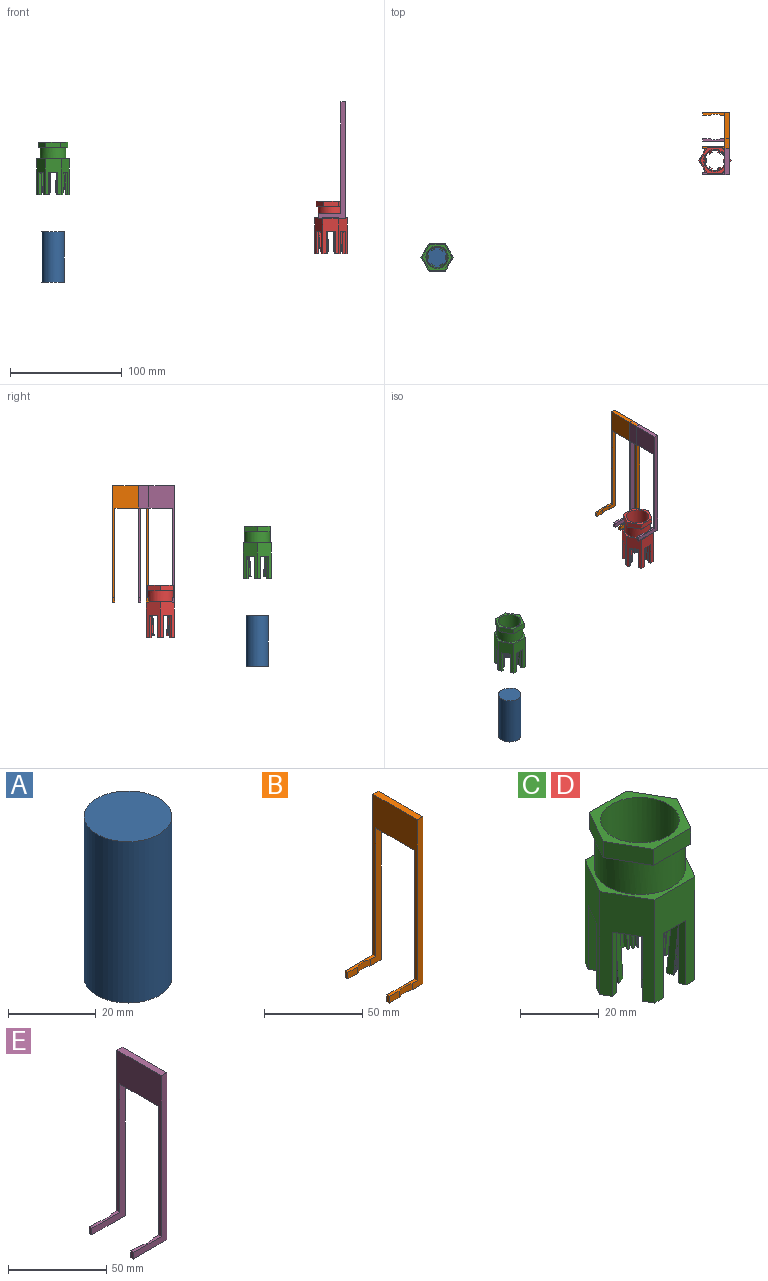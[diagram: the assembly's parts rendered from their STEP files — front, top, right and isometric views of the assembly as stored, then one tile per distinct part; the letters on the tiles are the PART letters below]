
ASSEMBLY  parts=5 mates=3
PART A: 3 faces, bbox 20x20x45 mm
  f0: cylinder r=10mm len=45mm, axis (0,0,-1), area 2827.4mm2, adj f1,f2
  f1: plane 20x20mm, normal (0,0,1), area 314.2mm2, adj f0
  f2: plane 20x20mm, normal (0,0,-1), area 314.2mm2, adj f0
PART B: 18 faces, bbox 24x32x104 mm
  f0: plane 84x7.81mm, normal (0,-1,0), area 351.2mm2, adj f1,f2,f6,f7,f8,f17
  f1: cylinder r=11.5mm len=9.38mm, axis (0,0,-1), area 38.7mm2, adj f0,f5,f6,f7
  f2: plane 104x32mm, normal (1,0,0), area 976mm2, adj f0,f3,f7,f9,f10,f14,f16,f17
  f3: plane 104x24mm, normal (0,1,0), area 496mm2, adj f2,f4,f6,f7,f8,f9
  f4: plane 4x2mm, normal (-1,0,0), area 8mm2, adj f3,f5,f6,f7
  f5: plane 6.81x4mm, normal (0,-1,0), area 27.2mm2, adj f1,f4,f6,f7
  f6: plane 20x2mm, normal (0,0,1), area 33.7mm2, adj f0,f1,f3,f4,f5,f8
  f7: plane 24x2mm, normal (0,0,-1), area 41.7mm2, adj f0,f1,f2,f3,f4,f5
  f8: plane 100x32mm, normal (-1,0,0), area 960mm2, adj f0,f3,f6,f9,f10,f14,f15,f17
  f9: plane 32x4mm, normal (0,0,1), area 128mm2, adj f2,f3,f8,f14
  f10: plane 84x24mm, normal (0,1,0), area 416mm2, adj f2,f8,f11,f15,f16,f17
  f11: plane 4x2mm, normal (-1,0,0), area 8mm2, adj f10,f12,f15,f16
  f12: plane 6.81x4mm, normal (0,-1,0), area 27.2mm2, adj f11,f13,f15,f16
  f13: cylinder r=11.5mm len=9.38mm, axis (0,0,-1), area 38.7mm2, adj f12,f14,f15,f16
  f14: plane 104x7.81mm, normal (0,-1,0), area 431.2mm2, adj f2,f8,f9,f13,f15,f16
  f15: plane 20x2mm, normal (0,0,1), area 33.7mm2, adj f8,f10,f11,f12,f13,f14
  f16: plane 24x2mm, normal (0,0,-1), area 41.7mm2, adj f2,f10,f11,f12,f13,f14
  f17: plane 28x4mm, normal (0,0,-1), area 112mm2, adj f0,f2,f8,f10
PART C: 256 faces, bbox 28.9x25x47 mm
  f0: plane 5.47x4.34mm, normal (0,0,-1), area 11.8mm2, adj f14,f17,f114,f115,f226,f239
  f1: plane 5.47x4.34mm, normal (0,0,-1), area 11.8mm2, adj f14,f16,f35,f37,f236,f241
  f2: cone r=9.54mm half-angle=5deg, axis (0,0,1), area 7.3mm2, adj f12,f16,f190,f241
  f3: plane 10x1.51mm, normal (0.98,-0.17,0), area 11mm2, adj f13,f18,f133,f240
  f4: plane 10x1.41mm, normal (-1,0.09,0), area 9.8mm2, adj f15,f18,f133,f240
  f5: plane 10x1.69mm, normal (-0.97,0.26,0), area 13.1mm2, adj f13,f17,f132,f240
  f6: plane 10x1.51mm, normal (0.98,0.17,0), area 11mm2, adj f10,f20,f135,f240
  f7: plane 10x1.69mm, normal (-0.97,-0.26,0), area 13.1mm2, adj f11,f20,f135,f240
  f8: plane 10x1.38mm, normal (1,0,0), area 9.4mm2, adj f15,f19,f134,f240
  f9: plane 10x1.41mm, normal (-1,-0.09,0), area 9.8mm2, adj f10,f19,f134,f240
  f10: cone r=10mm half-angle=5deg, axis (0,0,1), area 8.4mm2, adj f6,f9,f216,f240
  f11: cone r=10mm half-angle=5deg, axis (0,0,1), area 14.3mm2, adj f7,f12,f190,f216,f240,f241
  f12: cone r=7.55mm half-angle=85deg, axis (0,0,-1), area 0.7mm2, adj f2,f11,f190,f241
  f13: cone r=10mm half-angle=5deg, axis (0,0,1), area 8.4mm2, adj f3,f5,f216,f240
  f14: plane 32x14.43mm, normal (0,-1,0), area 301.9mm2, adj f0,f1,f35,f114,f217,f239,f240,f241
  f15: cone r=10mm half-angle=5deg, axis (0,0,1), area 8.4mm2, adj f4,f8,f216,f240
  f16: plane 30.04x2.75mm, normal (0,1,0), area 74mm2, adj f1,f2,f37,f120,f136,f137,f190,f191
  f17: plane 30x3.25mm, normal (0,1,0), area 78.7mm2, adj f0,f5,f115,f131,f132,f167,f168,f169
  f18: plane 10x0.93mm, normal (0,1,0), area 9.3mm2, adj f3,f4,f133,f240
  f19: plane 10x0.92mm, normal (0,1,0), area 9.2mm2, adj f8,f9,f134,f240
  f20: plane 10x0.96mm, normal (0,1,0), area 9.6mm2, adj f6,f7,f135,f240
  f21: plane 5.57x3.66mm, normal (0,0,-1), area 11.8mm2, adj f35,f36,f55,f57,f233,f238
  f22: cone r=9.54mm half-angle=5deg, axis (0,0,1), area 7.3mm2, adj f34,f36,f186,f238
  f23: plane 10x1.44mm, normal (0.34,0.94,0), area 11mm2, adj f32,f40,f141,f237
  f24: plane 10x1.69mm, normal (-0.26,-0.97,0), area 13.1mm2, adj f33,f40,f141,f237
  f25: plane 10x1.19mm, normal (0.5,0.87,0), area 9.4mm2, adj f31,f39,f140,f237
  f26: plane 10x1.28mm, normal (-0.42,-0.91,0), area 9.8mm2, adj f32,f39,f140,f237
  f27: plane 10x1.18mm, normal (0.64,0.77,0), area 11mm2, adj f30,f38,f139,f237
  f28: plane 10x1.16mm, normal (-0.57,-0.82,0), area 9.8mm2, adj f31,f38,f139,f237
  f29: plane 10x1.23mm, normal (-0.71,-0.71,0), area 13.1mm2, adj f30,f37,f138,f237
  f30: cone r=10mm half-angle=5deg, axis (0,0,1), area 8.4mm2, adj f27,f29,f216,f237
  f31: cone r=10mm half-angle=5deg, axis (0,0,1), area 8.4mm2, adj f25,f28,f216,f237
  f32: cone r=10mm half-angle=5deg, axis (0,0,1), area 8.4mm2, adj f23,f26,f216,f237
  f33: cone r=10mm half-angle=5deg, axis (0,0,1), area 14.3mm2, adj f24,f34,f186,f216,f237,f238
  f34: cone r=7.55mm half-angle=85deg, axis (0,0,-1), area 0.7mm2, adj f22,f33,f186,f238
  f35: plane 32x12.5mm, normal (0.87,-0.5,0), area 301.9mm2, adj f1,f14,f21,f55,f217,f236,f237,f238
  f36: plane 30.04x2.38mm, normal (-0.87,0.5,0), area 74mm2, adj f21,f22,f57,f122,f142,f143,f186,f187
  f37: plane 30x2.81mm, normal (-0.87,0.5,0), area 78.7mm2, adj f1,f16,f29,f121,f137,f138,f188,f189
  f38: plane 10x0.81mm, normal (-0.87,0.5,0), area 9.3mm2, adj f27,f28,f139,f237
  f39: plane 10x0.8mm, normal (-0.87,0.5,0), area 9.2mm2, adj f25,f26,f140,f237
  f40: plane 10x0.83mm, normal (-0.87,0.5,0), area 9.6mm2, adj f23,f24,f141,f237
  f41: plane 5.47x4.34mm, normal (0,0,-1), area 11.8mm2, adj f55,f56,f75,f77,f230,f235
  f42: cone r=9.54mm half-angle=5deg, axis (0,0,1), area 7.3mm2, adj f54,f56,f182,f235
  f43: plane 10x1.18mm, normal (-0.64,0.77,0), area 11mm2, adj f52,f60,f147,f234
  f44: plane 10x1.23mm, normal (0.71,-0.71,0), area 13.1mm2, adj f53,f60,f147,f234
  f45: plane 10x1.19mm, normal (-0.5,0.87,0), area 9.4mm2, adj f51,f59,f146,f234
  f46: plane 10x1.16mm, normal (0.57,-0.82,0), area 9.8mm2, adj f52,f59,f146,f234
  f47: plane 10x1.44mm, normal (-0.34,0.94,0), area 11mm2, adj f50,f58,f145,f234
  f48: plane 10x1.28mm, normal (0.42,-0.91,0), area 9.8mm2, adj f51,f58,f145,f234
  f49: plane 10x1.69mm, normal (0.26,-0.97,0), area 13.1mm2, adj f50,f57,f144,f234
  f50: cone r=10mm half-angle=5deg, axis (0,0,1), area 8.4mm2, adj f47,f49,f216,f234
  f51: cone r=10mm half-angle=5deg, axis (0,0,1), area 8.4mm2, adj f45,f48,f216,f234
  f52: cone r=10mm half-angle=5deg, axis (0,0,1), area 8.4mm2, adj f43,f46,f216,f234
  f53: cone r=10mm half-angle=5deg, axis (0,0,1), area 14.3mm2, adj f44,f54,f182,f216,f234,f235
  f54: cone r=7.55mm half-angle=85deg, axis (0,0,-1), area 0.7mm2, adj f42,f53,f182,f235
  f55: plane 32x12.5mm, normal (0.87,0.5,0), area 301.9mm2, adj f21,f35,f41,f75,f217,f233,f234,f235
  f56: plane 30.04x2.38mm, normal (-0.87,-0.5,0), area 74mm2, adj f41,f42,f77,f124,f148,f149,f182,f183
  f57: plane 30x2.81mm, normal (-0.87,-0.5,0), area 78.7mm2, adj f21,f36,f49,f123,f143,f144,f184,f185
  f58: plane 10x0.81mm, normal (-0.87,-0.5,0), area 9.3mm2, adj f47,f48,f145,f234
  f59: plane 10x0.8mm, normal (-0.87,-0.5,0), area 9.2mm2, adj f45,f46,f146,f234
  f60: plane 10x0.83mm, normal (-0.87,-0.5,0), area 9.6mm2, adj f43,f44,f147,f234
  f61: plane 5.47x4.34mm, normal (0,0,-1), area 11.8mm2, adj f75,f76,f95,f97,f227,f232
  f62: cone r=9.54mm half-angle=5deg, axis (0,0,1), area 7.3mm2, adj f74,f76,f178,f232
  f63: plane 10x1.51mm, normal (-0.98,-0.17,0), area 11mm2, adj f72,f80,f153,f231
  f64: plane 10x1.69mm, normal (0.97,0.26,0), area 13.1mm2, adj f73,f80,f153,f231
  f65: plane 10x1.38mm, normal (-1,0,0), area 9.4mm2, adj f71,f79,f152,f231
  f66: plane 10x1.41mm, normal (1,0.09,0), area 9.8mm2, adj f72,f79,f152,f231
  f67: plane 10x1.51mm, normal (-0.98,0.17,0), area 11mm2, adj f70,f78,f151,f231
  f68: plane 10x1.41mm, normal (1,-0.09,0), area 9.8mm2, adj f71,f78,f151,f231
  f69: plane 10x1.69mm, normal (0.97,-0.26,0), area 13.1mm2, adj f70,f77,f150,f231
  f70: cone r=10mm half-angle=5deg, axis (0,0,1), area 8.4mm2, adj f67,f69,f216,f231
  f71: cone r=10mm half-angle=5deg, axis (0,0,1), area 8.4mm2, adj f65,f68,f216,f231
  f72: cone r=10mm half-angle=5deg, axis (0,0,1), area 8.4mm2, adj f63,f66,f216,f231
  f73: cone r=10mm half-angle=5deg, axis (0,0,1), area 14.3mm2, adj f64,f74,f178,f216,f231,f232
  f74: cone r=7.55mm half-angle=85deg, axis (0,0,-1), area 0.7mm2, adj f62,f73,f178,f232
  f75: plane 32x14.43mm, normal (0,1,0), area 301.9mm2, adj f41,f55,f61,f95,f217,f230,f231,f232
  f76: plane 30.04x2.75mm, normal (0,-1,0), area 74mm2, adj f61,f62,f97,f126,f154,f155,f178,f179
  f77: plane 30x3.25mm, normal (0,-1,0), area 78.7mm2, adj f41,f56,f69,f125,f149,f150,f180,f181
  f78: plane 10x0.93mm, normal (0,-1,0), area 9.3mm2, adj f67,f68,f151,f231
  f79: plane 10x0.92mm, normal (0,-1,0), area 9.2mm2, adj f65,f66,f152,f231
  f80: plane 10x0.96mm, normal (0,-1,0), area 9.6mm2, adj f63,f64,f153,f231
  f81: plane 5.57x3.66mm, normal (0,0,-1), area 11.8mm2, adj f95,f96,f114,f116,f225,f229
  f82: cone r=9.54mm half-angle=5deg, axis (0,0,1), area 7.3mm2, adj f94,f96,f174,f229
  f83: plane 10x1.44mm, normal (-0.34,-0.94,0), area 11mm2, adj f92,f100,f159,f228
  f84: plane 10x1.69mm, normal (0.26,0.97,0), area 13.1mm2, adj f93,f100,f159,f228
  f85: plane 10x1.19mm, normal (-0.5,-0.87,0), area 9.4mm2, adj f91,f99,f158,f228
  f86: plane 10x1.28mm, normal (0.42,0.91,0), area 9.8mm2, adj f92,f99,f158,f228
  f87: plane 10x1.18mm, normal (-0.64,-0.77,0), area 11mm2, adj f90,f98,f157,f228
  f88: plane 10x1.16mm, normal (0.57,0.82,0), area 9.8mm2, adj f91,f98,f157,f228
  f89: plane 10x1.23mm, normal (0.71,0.71,0), area 13.1mm2, adj f90,f97,f156,f228
  f90: cone r=10mm half-angle=5deg, axis (0,0,1), area 8.4mm2, adj f87,f89,f216,f228
  f91: cone r=10mm half-angle=5deg, axis (0,0,1), area 8.4mm2, adj f85,f88,f216,f228
  f92: cone r=10mm half-angle=5deg, axis (0,0,1), area 8.4mm2, adj f83,f86,f216,f228
  f93: cone r=10mm half-angle=5deg, axis (0,0,1), area 14.3mm2, adj f84,f94,f174,f216,f228,f229
  f94: cone r=7.55mm half-angle=85deg, axis (0,0,-1), area 0.7mm2, adj f82,f93,f174,f229
  f95: plane 32x12.5mm, normal (-0.87,0.5,0), area 301.9mm2, adj f61,f75,f81,f114,f217,f227,f228,f229
  f96: plane 30.04x2.38mm, normal (0.87,-0.5,0), area 74mm2, adj f81,f82,f116,f128,f160,f161,f174,f175
  f97: plane 30x2.81mm, normal (0.87,-0.5,0), area 78.7mm2, adj f61,f76,f89,f127,f155,f156,f176,f177
  f98: plane 10x0.81mm, normal (0.87,-0.5,0), area 9.3mm2, adj f87,f88,f157,f228
  f99: plane 10x0.8mm, normal (0.87,-0.5,0), area 9.2mm2, adj f85,f86,f158,f228
  f100: plane 10x0.83mm, normal (0.87,-0.5,0), area 9.6mm2, adj f83,f84,f159,f228
  f101: cone r=9.54mm half-angle=5deg, axis (0,0,1), area 7.3mm2, adj f113,f115,f170,f226
  f102: plane 10x1.18mm, normal (0.64,-0.77,0), area 11mm2, adj f111,f119,f165,f224
  f103: plane 10x1.23mm, normal (-0.71,0.71,0), area 13.1mm2, adj f112,f119,f165,f224
  f104: plane 10x1.19mm, normal (0.5,-0.87,0), area 9.4mm2, adj f110,f118,f164,f224
  f105: plane 10x1.16mm, normal (-0.57,0.82,0), area 9.8mm2, adj f111,f118,f164,f224
  f106: plane 10x1.44mm, normal (0.34,-0.94,0), area 11mm2, adj f109,f117,f163,f224
  f107: plane 10x1.28mm, normal (-0.42,0.91,0), area 9.8mm2, adj f110,f117,f163,f224
  f108: plane 10x1.69mm, normal (-0.26,0.97,0), area 13.1mm2, adj f109,f116,f162,f224
  f109: cone r=10mm half-angle=5deg, axis (0,0,1), area 8.4mm2, adj f106,f108,f216,f224
  f110: cone r=10mm half-angle=5deg, axis (0,0,1), area 8.4mm2, adj f104,f107,f216,f224
  f111: cone r=10mm half-angle=5deg, axis (0,0,1), area 8.4mm2, adj f102,f105,f216,f224
  f112: cone r=10mm half-angle=5deg, axis (0,0,1), area 14.3mm2, adj f103,f113,f170,f216,f224,f226
  f113: cone r=7.55mm half-angle=85deg, axis (0,0,-1), area 0.7mm2, adj f101,f112,f170,f226
  f114: plane 32x12.5mm, normal (-0.87,-0.5,0), area 301.9mm2, adj f0,f14,f81,f95,f217,f224,f225,f226
  f115: plane 30.04x2.38mm, normal (0.87,0.5,0), area 74mm2, adj f0,f17,f101,f130,f166,f167,f170,f171
  f116: plane 30x2.81mm, normal (0.87,0.5,0), area 78.7mm2, adj f81,f96,f108,f129,f161,f162,f172,f173
  f117: plane 10x0.81mm, normal (0.87,0.5,0), area 9.3mm2, adj f106,f107,f163,f224
  f118: plane 10x0.8mm, normal (0.87,0.5,0), area 9.2mm2, adj f104,f105,f164,f224
  f119: plane 10x0.83mm, normal (0.87,0.5,0), area 9.6mm2, adj f102,f103,f165,f224
  f120: cone r=9.54mm half-angle=5deg, axis (0,0,1), area 24.6mm2, adj f16,f137,f191,f193,f223
  f121: cone r=9.54mm half-angle=5deg, axis (0,0,1), area 19.1mm2, adj f37,f188,f189,f195
  f122: cone r=9.54mm half-angle=5deg, axis (0,0,1), area 24.6mm2, adj f36,f143,f187,f197,f222
  f123: cone r=9.54mm half-angle=5deg, axis (0,0,1), area 19.1mm2, adj f57,f184,f185,f199
  f124: cone r=9.54mm half-angle=5deg, axis (0,0,1), area 24.6mm2, adj f56,f149,f183,f201,f221
  f125: cone r=9.54mm half-angle=5deg, axis (0,0,1), area 19.1mm2, adj f77,f180,f181,f203
  f126: cone r=9.54mm half-angle=5deg, axis (0,0,1), area 24.6mm2, adj f76,f155,f179,f205,f220
  f127: cone r=9.54mm half-angle=5deg, axis (0,0,1), area 19.1mm2, adj f97,f176,f177,f207
  f128: cone r=9.54mm half-angle=5deg, axis (0,0,1), area 24.6mm2, adj f96,f161,f175,f209,f219
  f129: cone r=9.54mm half-angle=5deg, axis (0,0,1), area 19.1mm2, adj f116,f172,f173,f211
  f130: cone r=9.54mm half-angle=5deg, axis (0,0,1), area 24.6mm2, adj f115,f167,f171,f213,f218
  f131: cone r=9.54mm half-angle=5deg, axis (0,0,1), area 19.1mm2, adj f17,f168,f169,f215
  f132: plane 1.23x1.1mm, normal (0,0,-1), area 0.9mm2, adj f5,f17,f168,f216
  f133: plane 0.98x0.65mm, normal (0,0,-1), area 0.5mm2, adj f3,f4,f18,f216
  f134: plane 0.92x0.54mm, normal (0,0,-1), area 0.5mm2, adj f8,f9,f19,f216
  f135: plane 1.08x0.84mm, normal (0,0,-1), area 0.7mm2, adj f6,f7,f20,f216
  f136: plane 1.48x1.44mm, normal (0,0,-1), area 1.3mm2, adj f16,f190,f191,f216
  f137: plane 2.31x1.65mm, normal (0,0,-1), area 1.8mm2, adj f16,f37,f120,f189,f216,f223
  f138: plane 1.49x1.26mm, normal (0,0,-1), area 0.9mm2, adj f29,f37,f188,f216
  f139: plane 1.12x0.97mm, normal (0,0,-1), area 0.5mm2, adj f27,f28,f38,f216
  f140: plane 1.02x0.89mm, normal (0,0,-1), area 0.5mm2, adj f25,f26,f39,f216
  f141: plane 1.1x1.06mm, normal (0,0,-1), area 0.7mm2, adj f23,f24,f40,f216
  f142: plane 1.69x1.07mm, normal (0,0,-1), area 1.3mm2, adj f36,f186,f187,f216
  f143: plane 2.16x1.22mm, normal (0,0,-1), area 1.8mm2, adj f36,f57,f122,f185,f216,f222
  f144: plane 1.35x1.08mm, normal (0,0,-1), area 0.9mm2, adj f49,f57,f184,f216
  f145: plane 1.03x0.96mm, normal (0,0,-1), area 0.5mm2, adj f47,f48,f58,f216
  f146: plane 1.05x0.9mm, normal (0,0,-1), area 0.5mm2, adj f45,f46,f59,f216
  f147: plane 1.26x1.1mm, normal (0,0,-1), area 0.7mm2, adj f43,f44,f60,f216
  f148: plane 1.83x1.45mm, normal (0,0,-1), area 1.3mm2, adj f56,f182,f183,f216
  f149: plane 1.95x1.84mm, normal (0,0,-1), area 1.8mm2, adj f56,f77,f124,f181,f216,f221
  f150: plane 1.23x1.1mm, normal (0,0,-1), area 0.9mm2, adj f69,f77,f180,f216
  f151: plane 0.98x0.65mm, normal (0,0,-1), area 0.5mm2, adj f67,f68,f78,f216
  f152: plane 0.92x0.54mm, normal (0,0,-1), area 0.5mm2, adj f65,f66,f79,f216
  f153: plane 1.08x0.84mm, normal (0,0,-1), area 0.7mm2, adj f63,f64,f80,f216
  f154: plane 1.48x1.44mm, normal (0,0,-1), area 1.3mm2, adj f76,f178,f179,f216
  f155: plane 2.31x1.65mm, normal (0,0,-1), area 1.8mm2, adj f76,f97,f126,f177,f216,f220
  f156: plane 1.49x1.26mm, normal (0,0,-1), area 0.9mm2, adj f89,f97,f176,f216
  f157: plane 1.12x0.97mm, normal (0,0,-1), area 0.5mm2, adj f87,f88,f98,f216
  f158: plane 1.02x0.89mm, normal (0,0,-1), area 0.5mm2, adj f85,f86,f99,f216
  f159: plane 1.1x1.06mm, normal (0,0,-1), area 0.7mm2, adj f83,f84,f100,f216
  f160: plane 1.69x1.07mm, normal (0,0,-1), area 1.3mm2, adj f96,f174,f175,f216
  f161: plane 2.16x1.22mm, normal (0,0,-1), area 1.8mm2, adj f96,f116,f128,f173,f216,f219
  f162: plane 1.35x1.08mm, normal (0,0,-1), area 0.9mm2, adj f108,f116,f172,f216
  f163: plane 1.03x0.96mm, normal (0,0,-1), area 0.5mm2, adj f106,f107,f117,f216
  f164: plane 1.05x0.9mm, normal (0,0,-1), area 0.5mm2, adj f104,f105,f118,f216
  f165: plane 1.26x1.1mm, normal (0,0,-1), area 0.7mm2, adj f102,f103,f119,f216
  f166: plane 1.83x1.45mm, normal (0,0,-1), area 1.3mm2, adj f115,f170,f171,f216
  f167: plane 1.95x1.84mm, normal (0,0,-1), area 1.8mm2, adj f17,f115,f130,f169,f216,f218
  f168: plane 28.17x3.41mm, normal (0.94,-0.34,0), area 52.4mm2, adj f17,f131,f132,f214,f215
  f169: plane 28.17x3.66mm, normal (-0.91,0.42,0), area 55.4mm2, adj f17,f131,f167,f214,f215
  f170: plane 28.17x2.78mm, normal (0.77,-0.64,0), area 52.4mm2, adj f101,f112,f113,f115,f166
  f171: plane 28.17x3.31mm, normal (-0.82,0.57,0), area 55.4mm2, adj f115,f130,f166,f212,f213
  f172: plane 28.17x3.57mm, normal (0.17,-0.98,0), area 52.4mm2, adj f116,f129,f162,f210,f211
  f173: plane 28.17x4.02mm, normal (-0.09,1,0), area 55.4mm2, adj f116,f129,f161,f210,f211
  f174: plane 28.17x3.57mm, normal (-0.17,-0.98,0), area 52.4mm2, adj f82,f93,f94,f96,f160
  f175: plane 28.17x4.02mm, normal (0.09,1,0), area 55.4mm2, adj f96,f128,f160,f208,f209
  f176: plane 28.17x2.78mm, normal (-0.77,-0.64,0), area 52.4mm2, adj f97,f127,f156,f206,f207
  f177: plane 28.17x3.31mm, normal (0.82,0.57,0), area 55.4mm2, adj f97,f127,f155,f206,f207
  f178: plane 28.17x3.41mm, normal (-0.94,-0.34,0), area 52.4mm2, adj f62,f73,f74,f76,f154
  f179: plane 28.17x3.66mm, normal (0.91,0.42,0), area 55.4mm2, adj f76,f126,f154,f204,f205
  f180: plane 28.17x3.41mm, normal (-0.94,0.34,0), area 52.4mm2, adj f77,f125,f150,f202,f203
  f181: plane 28.17x3.66mm, normal (0.91,-0.42,0), area 55.4mm2, adj f77,f125,f149,f202,f203
  f182: plane 28.17x2.78mm, normal (-0.77,0.64,0), area 52.4mm2, adj f42,f53,f54,f56,f148
  f183: plane 28.17x3.31mm, normal (0.82,-0.57,0), area 55.4mm2, adj f56,f124,f148,f200,f201
  f184: plane 28.17x3.57mm, normal (-0.17,0.98,0), area 52.4mm2, adj f57,f123,f144,f198,f199
  f185: plane 28.17x4.02mm, normal (0.09,-1,0), area 55.4mm2, adj f57,f123,f143,f198,f199
  f186: plane 28.17x3.57mm, normal (0.17,0.98,0), area 52.4mm2, adj f22,f33,f34,f36,f142
  f187: plane 28.17x4.02mm, normal (-0.09,-1,0), area 55.4mm2, adj f36,f122,f142,f196,f197
  f188: plane 28.17x2.78mm, normal (0.77,0.64,0), area 52.4mm2, adj f37,f121,f138,f194,f195
  f189: plane 28.17x3.31mm, normal (-0.82,-0.57,0), area 55.4mm2, adj f37,f121,f137,f194,f195
  f190: plane 28.17x3.41mm, normal (0.94,0.34,0), area 52.4mm2, adj f2,f11,f12,f16,f136
  f191: plane 28.17x3.66mm, normal (-0.91,-0.42,0), area 55.4mm2, adj f16,f120,f136,f192,f193
  f192: cone r=10mm half-angle=5deg, axis (0,0,1), area 21.5mm2, adj f191,f193,f216,f223
  f193: cone r=7.55mm half-angle=85deg, axis (0,0,-1), area 1.5mm2, adj f120,f191,f192,f223
  f194: cone r=10mm half-angle=5deg, axis (0,0,1), area 21.5mm2, adj f188,f189,f195,f216
  f195: cone r=7.55mm half-angle=85deg, axis (0,0,-1), area 1.5mm2, adj f121,f188,f189,f194
  f196: cone r=10mm half-angle=5deg, axis (0,0,1), area 21.5mm2, adj f187,f197,f216,f222
  f197: cone r=7.55mm half-angle=85deg, axis (0,0,-1), area 1.5mm2, adj f122,f187,f196,f222
  f198: cone r=10mm half-angle=5deg, axis (0,0,1), area 21.5mm2, adj f184,f185,f199,f216
  f199: cone r=7.55mm half-angle=85deg, axis (0,0,-1), area 1.5mm2, adj f123,f184,f185,f198
  f200: cone r=10mm half-angle=5deg, axis (0,0,1), area 21.5mm2, adj f183,f201,f216,f221
  f201: cone r=7.55mm half-angle=85deg, axis (0,0,-1), area 1.5mm2, adj f124,f183,f200,f221
  f202: cone r=10mm half-angle=5deg, axis (0,0,1), area 21.5mm2, adj f180,f181,f203,f216
  f203: cone r=7.55mm half-angle=85deg, axis (0,0,-1), area 1.5mm2, adj f125,f180,f181,f202
  f204: cone r=10mm half-angle=5deg, axis (0,0,1), area 21.5mm2, adj f179,f205,f216,f220
  f205: cone r=7.55mm half-angle=85deg, axis (0,0,-1), area 1.5mm2, adj f126,f179,f204,f220
  f206: cone r=10mm half-angle=5deg, axis (0,0,1), area 21.5mm2, adj f176,f177,f207,f216
  f207: cone r=7.55mm half-angle=85deg, axis (0,0,-1), area 1.5mm2, adj f127,f176,f177,f206
  f208: cone r=10mm half-angle=5deg, axis (0,0,1), area 21.5mm2, adj f175,f209,f216,f219
  f209: cone r=7.55mm half-angle=85deg, axis (0,0,-1), area 1.5mm2, adj f128,f175,f208,f219
  f210: cone r=10mm half-angle=5deg, axis (0,0,1), area 21.5mm2, adj f172,f173,f211,f216
  f211: cone r=7.55mm half-angle=85deg, axis (0,0,-1), area 1.5mm2, adj f129,f172,f173,f210
  f212: cone r=10mm half-angle=5deg, axis (0,0,1), area 21.5mm2, adj f171,f213,f216,f218
  f213: cone r=7.55mm half-angle=85deg, axis (0,0,-1), area 1.5mm2, adj f130,f171,f212,f218
  f214: cone r=10mm half-angle=5deg, axis (0,0,1), area 21.5mm2, adj f168,f169,f215,f216
  f215: cone r=7.55mm half-angle=85deg, axis (0,0,-1), area 1.5mm2, adj f131,f168,f169,f214
  f216: cylinder r=10mm len=20mm, axis (0,0,1), area 1068.1mm2, adj f10,f11,f13,f15,f30,f31,f32,f33
  f217: plane 28.87x25mm, normal (0,0,1), area 125.8mm2, adj f14,f35,f55,f75,f95,f114,f242
  f218: plane 28.17x3.86mm, normal (0.87,-0.5,0), area 56.4mm2, adj f130,f167,f212,f213
  f219: plane 28.17x4.46mm, normal (0,-1,0), area 56.4mm2, adj f128,f161,f208,f209
  f220: plane 28.17x3.86mm, normal (-0.87,-0.5,0), area 56.4mm2, adj f126,f155,f204,f205
  f221: plane 28.17x3.86mm, normal (-0.87,0.5,0), area 56.4mm2, adj f124,f149,f200,f201
  f222: plane 28.17x4.46mm, normal (0,1,0), area 56.4mm2, adj f122,f143,f196,f197
  f223: plane 28.17x3.86mm, normal (0.87,0.5,0), area 56.4mm2, adj f120,f137,f192,f193
  f224: plane 7.37x6.69mm, normal (0,0,-1), area 19.5mm2, adj f102,f103,f104,f105,f106,f107,f108,f109
  f225: plane 20x2.05mm, normal (0.21,-0.98,0), area 42mm2, adj f81,f114,f116,f224
  f226: plane 20x4.13mm, normal (-0.74,0.67,0), area 78.2mm2, adj f0,f101,f112,f113,f114,f115,f224
  f227: plane 20x1.55mm, normal (-0.74,-0.67,0), area 42mm2, adj f61,f95,f97,f228
  f228: plane 7.78x6.37mm, normal (0,0,-1), area 19.5mm2, adj f83,f84,f85,f86,f87,f88,f89,f90
  f229: plane 20x5.45mm, normal (0.21,0.98,0), area 78.2mm2, adj f81,f82,f93,f94,f95,f96,f228
  f230: plane 20x2mm, normal (-0.95,0.3,0), area 42mm2, adj f41,f75,f77,f231
  f231: plane 8x3.81mm, normal (0,0,-1), area 19.5mm2, adj f63,f64,f65,f66,f67,f68,f69,f70
  f232: plane 20x5.31mm, normal (0.95,0.3,0), area 78.2mm2, adj f61,f62,f73,f74,f75,f76,f231
  f233: plane 20x2.05mm, normal (-0.21,0.98,0), area 42mm2, adj f21,f55,f57,f234
  f234: plane 7.37x6.69mm, normal (0,0,-1), area 19.5mm2, adj f43,f44,f45,f46,f47,f48,f49,f50
  f235: plane 20x4.13mm, normal (0.74,-0.67,0), area 78.2mm2, adj f41,f42,f53,f54,f55,f56,f234
  f236: plane 20x1.55mm, normal (0.74,0.67,0), area 42mm2, adj f1,f35,f37,f237
  f237: plane 7.78x6.37mm, normal (0,0,-1), area 19.5mm2, adj f23,f24,f25,f26,f27,f28,f29,f30
  f238: plane 20x5.45mm, normal (-0.21,-0.98,0), area 78.2mm2, adj f21,f22,f33,f34,f35,f36,f237
  f239: plane 20x2mm, normal (0.95,-0.3,0), area 42mm2, adj f0,f14,f17,f240
  f240: plane 8x3.81mm, normal (0,0,-1), area 19.5mm2, adj f3,f4,f5,f6,f7,f8,f9,f10
  f241: plane 20x5.31mm, normal (-0.95,-0.3,0), area 78.2mm2, adj f1,f2,f11,f12,f14,f16,f240
  f242: cylinder r=11.5mm len=23mm, axis (0,0,-1), area 722.6mm2, adj f217,f243,f244,f245,f246,f247,f248
  f243: plane 9.96x5.75mm, normal (0,0,-1), area 7.1mm2, adj f242,f249,f254
  f244: plane 9.96x5.75mm, normal (0,0,-1), area 7.1mm2, adj f242,f249,f250
  f245: plane 11.5x3.32mm, normal (0,0,-1), area 7.1mm2, adj f242,f250,f251
  f246: plane 9.96x5.75mm, normal (0,0,-1), area 7.1mm2, adj f242,f251,f252
  f247: plane 9.96x5.75mm, normal (0,0,-1), area 7.1mm2, adj f242,f252,f253
  f248: plane 11.5x3.32mm, normal (0,0,-1), area 7.1mm2, adj f242,f253,f254
  f249: plane 13.28x5mm, normal (0,1,0), area 66.4mm2, adj f243,f244,f250,f254,f255
  f250: plane 11.5x6.64mm, normal (-0.87,0.5,0), area 66.4mm2, adj f244,f245,f249,f251,f255
  f251: plane 11.5x6.64mm, normal (-0.87,-0.5,0), area 66.4mm2, adj f245,f246,f250,f252,f255
  f252: plane 13.28x5mm, normal (0,-1,0), area 66.4mm2, adj f246,f247,f251,f253,f255
  f253: plane 11.5x6.64mm, normal (0.87,-0.5,0), area 66.4mm2, adj f247,f248,f252,f254,f255
  f254: plane 11.5x6.64mm, normal (0.87,0.5,0), area 66.4mm2, adj f243,f248,f249,f253,f255
  f255: plane 26.56x23mm, normal (0,0,1), area 144mm2, adj f216,f249,f250,f251,f252,f253,f254
PART D: same geometry as C
PART E: 18 faces, bbox 24x32x104 mm
  f0: plane 84x7.81mm, normal (0,1,0), area 351.2mm2, adj f1,f2,f6,f7,f8,f17
  f1: cylinder r=11.5mm len=9.38mm, axis (0,0,-1), area 38.7mm2, adj f0,f5,f6,f7
  f2: plane 104x32mm, normal (1,0,0), area 976mm2, adj f0,f3,f7,f9,f10,f14,f16,f17
  f3: plane 104x24mm, normal (0,-1,0), area 496mm2, adj f2,f4,f6,f7,f8,f9
  f4: plane 4x2mm, normal (-1,0,0), area 8mm2, adj f3,f5,f6,f7
  f5: plane 6.81x4mm, normal (0,1,0), area 27.2mm2, adj f1,f4,f6,f7
  f6: plane 20x2mm, normal (0,0,1), area 33.7mm2, adj f0,f1,f3,f4,f5,f8
  f7: plane 24x2mm, normal (0,0,-1), area 41.7mm2, adj f0,f1,f2,f3,f4,f5
  f8: plane 100x32mm, normal (-1,0,0), area 960mm2, adj f0,f3,f6,f9,f10,f14,f15,f17
  f9: plane 32x4mm, normal (0,0,1), area 128mm2, adj f2,f3,f8,f14
  f10: plane 84x24mm, normal (0,-1,0), area 416mm2, adj f2,f8,f11,f15,f16,f17
  f11: plane 4x2mm, normal (-1,0,0), area 8mm2, adj f10,f12,f15,f16
  f12: plane 6.81x4mm, normal (0,1,0), area 27.2mm2, adj f11,f13,f15,f16
  f13: cylinder r=11.5mm len=9.38mm, axis (0,0,-1), area 38.7mm2, adj f12,f14,f15,f16
  f14: plane 104x7.81mm, normal (0,1,0), area 431.2mm2, adj f2,f8,f9,f13,f15,f16
  f15: plane 20x2mm, normal (0,0,1), area 33.7mm2, adj f8,f10,f11,f12,f13,f14
  f16: plane 24x2mm, normal (0,0,-1), area 41.7mm2, adj f2,f10,f11,f12,f13,f14
  f17: plane 28x4mm, normal (0,0,-1), area 112mm2, adj f0,f2,f8,f10
PLACE A t=(-157.32,-102.18,-180.62)mm
PLACE B t=(111.37,49.95,-123.35)mm
PLACE C t=(-106.97,-100.57,-70.28)mm
PLACE D t=(141.51,-13.88,-123.12)mm
PLACE E t=(111.37,-47.71,-123.35)mm
MATE planar B.f2 <-> E.f2  axis (1,0,0) through (154.48,12.71,-19.35)mm
MATE planar B.f16 <-> E.f16  axis (0,0,-1) through (142.55,-2.2,-123.35)mm
MATE slider C.f216 <-> A.f0  axis (0,0,1) through (-106.97,-100.57,-55.28)mm
